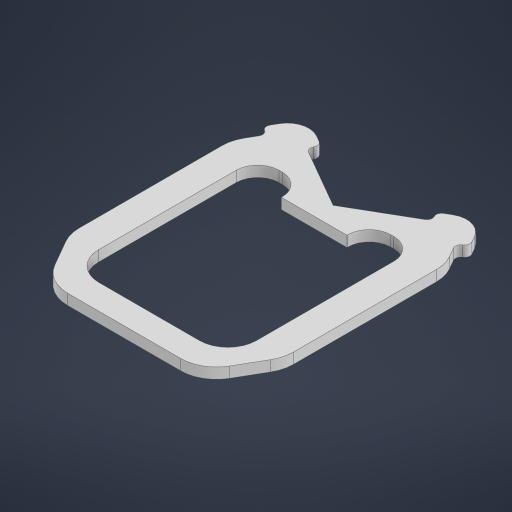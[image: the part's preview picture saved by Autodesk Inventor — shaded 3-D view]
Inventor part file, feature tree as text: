
AUTODESK INVENTOR PART (.ipt)
format: ipt  version: 2023 (Build 270158000, 158)  size: 460,800 bytes
history: native  units: in
note: dims shown in document units (in); Inventor stores cm internally (conversion verified against a paired STEP export)
features: extrude x8, chamfer x4, sketch x3, fillet x2, draft x1, direct_edit x1, move_body x1
ambient origin geometry x8: Origin, YZ Plane, XZ Plane, XY Plane, X Axis, Y Axis, Z Axis, Center Point
bodies: Solid1 (feature_tree)
feature tree (20):
  extrude  "Extrusion1"  Depth=0.1181in
  extrude  "Extrusion2"  Depth=0.3937in TaperAngle=0.0deg
  extrude  "Extrusion3"  Depth=0.1181in
  extrude  "Extrusion4"  Depth=0.315in
  extrude  "Extrusion5"  Depth=0.2362in
  chamfer  "Chamfer1"  Distance=0.2362in
  chamfer  "Chamfer2"  Distance=0.5689in
  chamfer  "Chamfer3"  Distance=0.0787in
  sketch  "Sketch2"  dims[d1=0.374in d3=120.0deg d4=60.0deg d5=0.1772in d6=2.9528in d11=0.0886in d14=60.0deg d15=0.1772in d16=0.0886in d17=1.5748in d18=0.1181in]
  fillet  "Fillet3"  Radius=0.0787in
  extrude  "Extrusion7"  Depth=0.315in
  draft  "FaceDraft3"
  fillet  "Fillet10"  Radius=0.0197in
  chamfer  "Chamfer8"  Distance=0.0394in
  extrude  "Extrusion10"  Depth=0.2362in
  direct_edit  "Direct Edit3"
  extrude  "Extrusion11"  TaperAngle=0.0deg  [1 undecoded]
  sketch  "Sketch7"  dims[d19=0.3937in d20=0.1969in d21=0.0in]
  sketch  "Sketch8"  dims[d22=0.2657in d24=0.1181in d25=0.315in d26=0.2362in d27=0.2362in d28=0.5689in d29=0.0787in d30=0.0787in d31=0.0787in d32=0.0197in d33=0.0in d34=0.0394in d35=0.0in d36=0.2362in d37=0.0in d38=0.0in d39=0.0in d40=0.0in d41=0.0in d42=0.0591in d43=0.2362in d44=0.0in d45=0.2756in d46=0.0492in d47=0.0in d48=0.2756in d49=0.0098in d50=45.0deg d52=0.0394in d53=0.1575in d54=75.0deg d55=0.0394in d56=0.1575in d57=75.0deg d66=0.315in d67=0.3937in d72=0.1575in d73=0.0in d74=45.0deg d105=0.315in d106=0.0787in d107=0.0787in d108=0.2405in d109=0.0787in d110=0.0in d111=0.0in d112=0.0in d113=0.1969in d114=0.7874in d115=0.0in d51=0.0in d59=0.0in d60=0.0in d61=0.0in d62=0.0in d63=0.0in d64=0.0in d65=0.0in d68=0.0344in d69=0.0197in d70=0.0344in d104=0.0in]
  move_body  "Move5"
note: 1 required parameter value undecoded (feature->parameter linkage not recoverable at this tier; creation-order binding heuristic only, values carry confidence <= 0.55)
